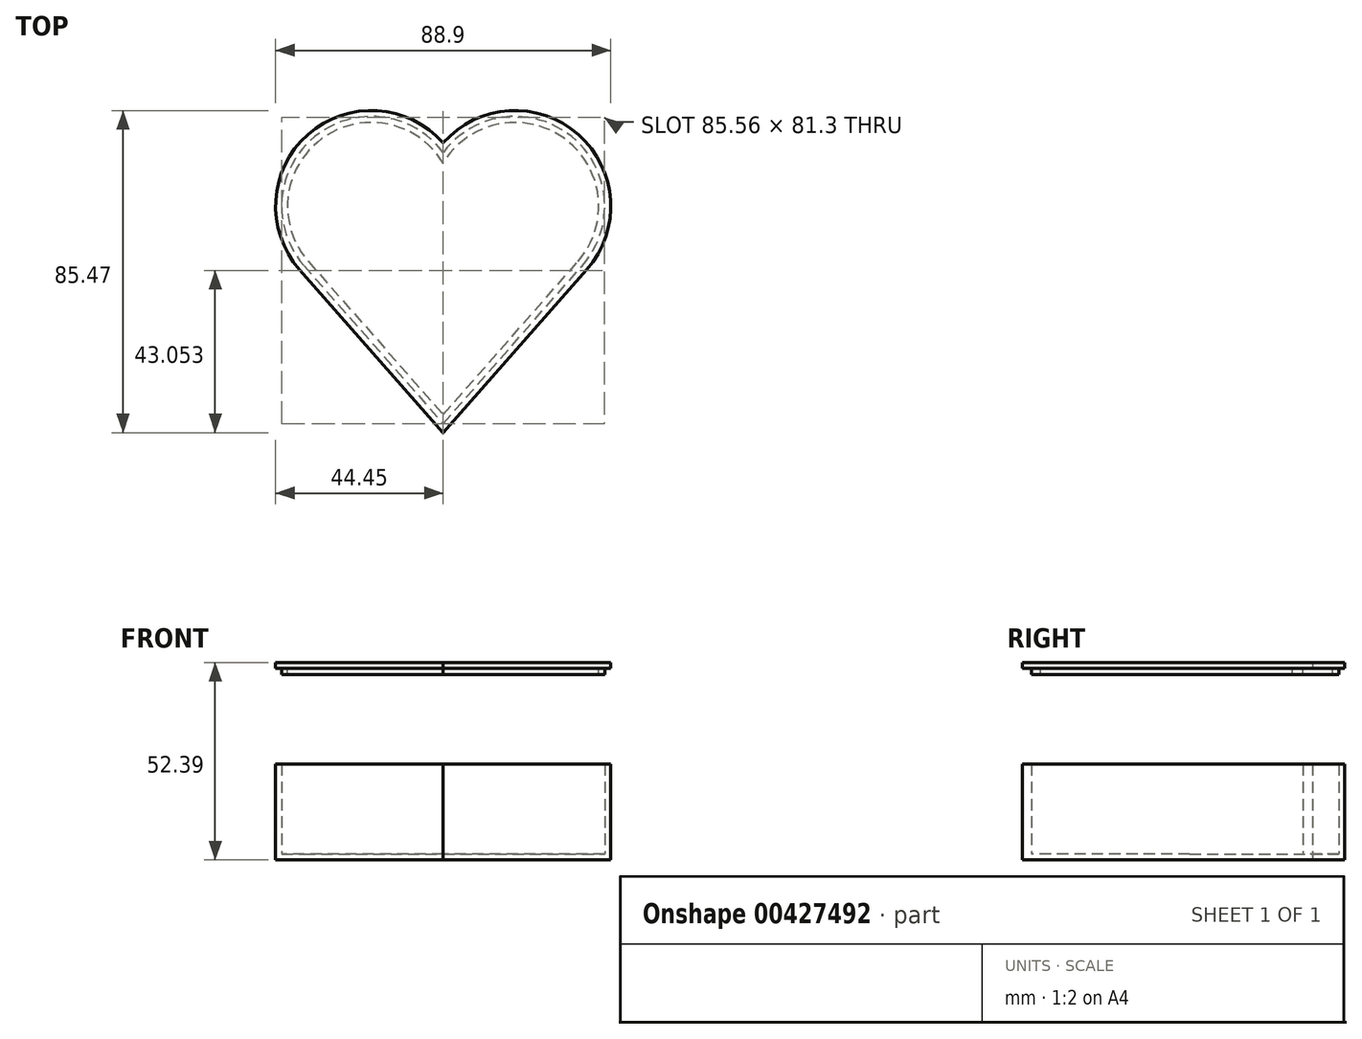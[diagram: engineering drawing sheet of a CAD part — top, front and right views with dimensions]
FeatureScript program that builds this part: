
annotation { "Feature Type Name" : "Feature", "Feature Type Description" : "" }
export const myFeature = defineFeature(function(context is Context, id is Id, definition is map)
    precondition{}
    {
        {
            var Q0;
            Q0=qCreatedBy(makeId("Top.planeOp"),FACE);
            var sketch = newSketch(context, id + "F0", { "sketchPlane" : qUnion([Q0])});
            skArc(sketch, "E0", {"start": v(0, 16.8) * mm, "mid": v(-35.84, 19.06) * mm, "end": v(-38.11, -16.79) * mm});
            skArc(sketch, "E1", {"start": v(38.11, -16.79) * mm, "mid": v(35.84, 19.06) * mm, "end": v(0, 16.8) * mm});
            skLineSegment(sketch, "E2", {"start": v(-38.11, -16.79) * mm, "end": v(0, -60.07) * mm});
            skLineSegment(sketch, "E3", {"start": v(0, -60.07) * mm, "end": v(38.11, -16.79) * mm});
            skSolve(sketch);
        }
        {
            var Q0;
            Q0=qSketchRegion(id+"F0",true);
            extrude(context, id + "F1", {"entities" : qUnion([Q0]), "depth" : 25.4 * mm});
        }
        {
            var Q0;
            Q0=makeQuery(id+"F1.opExtrude","CAP_FACE",FACE,{"disambiguationData":[OSD([sQuery(id+"F0.wireOp",EDGE,"E0"),sQuery(id+"F0.wireOp",EDGE,"E1"),sQuery(id+"F0.wireOp",EDGE,"E2"),sQuery(id+"F0.wireOp",EDGE,"E3")])],"isStart":false});
            shell(context, id + "F2", {"entities" : qUnion([Q0]), "thickness" : 1.59 * mm});
        }
        {
            var Q0;
            Q0=makeQuery(id+"F1.opExtrude","SWEPT_BODY",BODY,{"disambiguationData":[OSD([sQuery(id+"F0.wireOp",EDGE,"E0"),sQuery(id+"F0.wireOp",EDGE,"E1"),sQuery(id+"F0.wireOp",EDGE,"E2"),sQuery(id+"F0.wireOp",EDGE,"E3")])]});
            transform(context, id + "F3", {"entities" : qUnion([Q0]), "transformType" : TransformType.TRANSLATION_3D, "dx" : 0 * mm, "dy" : 0 * mm, "dz" : 0 * mm, "makeCopy" : true});
        }
        {
            var Q0;
            Q0=makeQuery(id+"F1.opExtrude","CAP_FACE",FACE,{"disambiguationData":[OSD([sQuery(id+"F0.wireOp",EDGE,"E0"),sQuery(id+"F0.wireOp",EDGE,"E1"),sQuery(id+"F0.wireOp",EDGE,"E2"),sQuery(id+"F0.wireOp",EDGE,"E3")])],"isStart":false});
            cPlane(context, id + "F4", {"entities" : qUnion([Q0]), "cplaneType" : CPlaneType.OFFSET, "offset" : 25.4 * mm, "width" : 152.4 * mm, "height" : 152.4 * mm});
        }
        {
            var Q0;
            Q0=qCreatedBy(id+"F4.planeOp",FACE);
            var sketch = newSketch(context, id + "F5", { "sketchPlane" : qUnion([Q0])});
            skArc(sketch, "E4.0", {"start": v(0, 16.8) * mm, "mid": v(-35.84, 19.06) * mm, "end": v(-38.11, -16.79) * mm});
            skArc(sketch, "E4.1", {"start": v(38.11, -16.79) * mm, "mid": v(35.84, 19.06) * mm, "end": v(0, 16.8) * mm});
            skLineSegment(sketch, "E4.2", {"start": v(0, -60.07) * mm, "end": v(38.11, -16.79) * mm});
            skLineSegment(sketch, "E4.3", {"start": v(-38.11, -16.79) * mm, "end": v(0, -60.07) * mm});
            skSolve(sketch);
        }
        {
            var Q0;
            Q0=qSketchRegion(id+"F5",true);
            extrude(context, id + "F6", {"entities" : qUnion([Q0]), "depth" : 1.59 * mm});
        }
        {
            var Q0;
            Q0=makeQuery(id+"F6.opExtrude","CAP_FACE",FACE,{"disambiguationData":[OSD([sQuery(id+"F5.wireOp",EDGE,"E4.0"),sQuery(id+"F5.wireOp",EDGE,"E4.1"),sQuery(id+"F5.wireOp",EDGE,"E4.2"),sQuery(id+"F5.wireOp",EDGE,"E4.3")])],"isStart":true});
            var sketch = newSketch(context, id + "F7", { "sketchPlane" : qUnion([Q0])});
            skArc(sketch, "E5.0", {"start": v(36.92, 15.74) * mm, "mid": v(34.07, -18.48) * mm, "end": v(0, -14.29) * mm});
            skArc(sketch, "E5.1", {"start": v(0, -14.29) * mm, "mid": v(-34.07, -18.48) * mm, "end": v(-36.92, 15.74) * mm});
            skLineSegment(sketch, "E5.2", {"start": v(0, 57.67) * mm, "end": v(36.92, 15.74) * mm});
            skLineSegment(sketch, "E5.3", {"start": v(-36.92, 15.74) * mm, "end": v(0, 57.67) * mm});
            skArc(sketch, "E6.0", {"start": v(0, -11.45) * mm, "mid": v(-32.17, -17.94) * mm, "end": v(-35.73, 14.69) * mm});
            skArc(sketch, "E6.1", {"start": v(35.73, 14.69) * mm, "mid": v(32.17, -17.94) * mm, "end": v(0, -11.45) * mm});
            skLineSegment(sketch, "E6.2", {"start": v(0, 55.27) * mm, "end": v(35.73, 14.69) * mm});
            skLineSegment(sketch, "E6.3", {"start": v(-35.73, 14.69) * mm, "end": v(0, 55.27) * mm});
            skSolve(sketch);
        }
        {
            var Q0;
            Q0=qSketchRegion(id+"F7",true);
            extrude(context, id + "F8", {"entities" : qUnion([Q0]), "operationType" : NewBodyOperationType.ADD, "depth" : 1.59 * mm});
        }
    });
